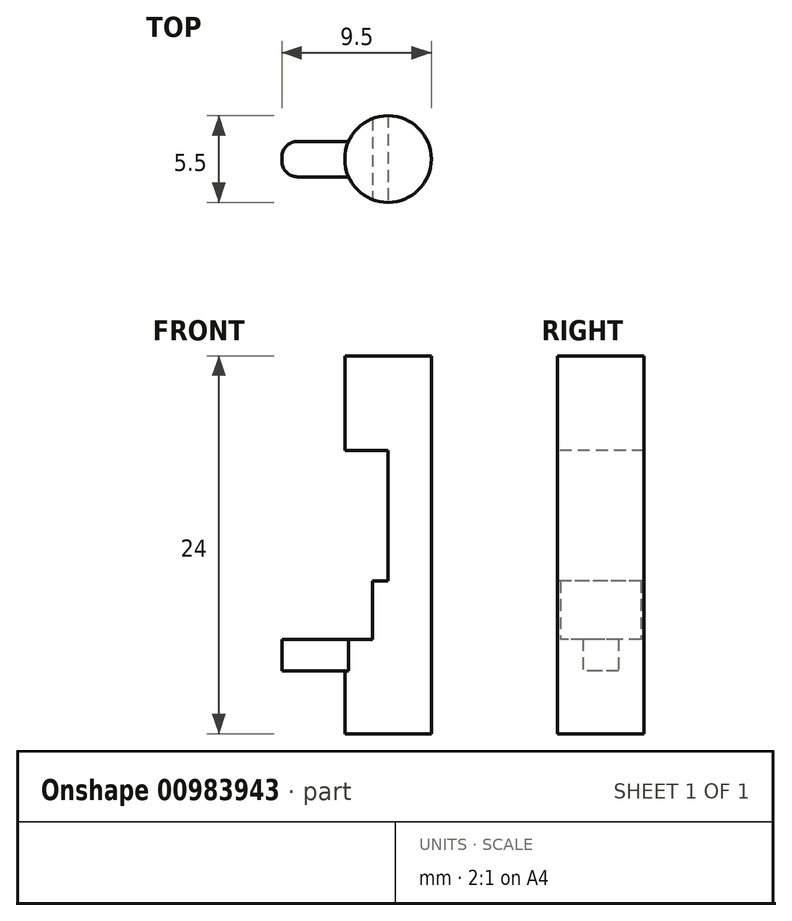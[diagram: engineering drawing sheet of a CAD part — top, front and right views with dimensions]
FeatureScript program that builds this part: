
annotation { "Feature Type Name" : "Feature", "Feature Type Description" : "" }
export const myFeature = defineFeature(function(context is Context, id is Id, definition is map)
    precondition{}
    {
        {
            var Q0;
            Q0=qCreatedBy(makeId("Top.planeOp"),FACE);
            var sketch = newSketch(context, id + "F0", { "sketchPlane" : qUnion([Q0])});
            skCircle(sketch, "E0", {"center": v(0, 0) * mm, "radius": 2.75 * mm});
            skLineSegment(sketch, "E1", {"start": v(0, 2.75) * mm, "end": v(0, -2.75) * mm});
            skLineSegment(sketch, "E2", {"start": v(-1, 2.56) * mm, "end": v(-1, -2.56) * mm});
            skLineSegment(sketch, "E3", {"start": v(0, 0) * mm, "end": v(0, 1.12) * mm});
            skLineSegment(sketch, "E4", {"start": v(0, 1.12) * mm, "end": v(-6.75, 1.12) * mm});
            skLineSegment(sketch, "E5", {"start": v(-6.75, 1.12) * mm, "end": v(-6.75, -1.13) * mm});
            skLineSegment(sketch, "E6", {"start": v(-6.75, -1.13) * mm, "end": v(0, -1.13) * mm});
            skSolve(sketch);
        }
        {
            var Q0;
            {var subQ0=sQuery(id+"F0.wireOp",EDGE,"E1");var subQ1=makeQuery(id+"F0.imprint","IMPRINT",VERTEX,{"derivedFrom":subQ0});Q0=makeQuery(id+"F0.imprint","IMPRINT",FACE,{"disambiguationData":[TD([[makeQuery(id+"F0.imprint","IMPRINT",EDGE,{"disambiguationData":[TD([[subQ1,-1.0]])],"derivedFrom":subQ0}),1.0]])]});}
            var Q1;
            {var subQ0=sQuery(id+"F0.wireOp",EDGE,"E2");var subQ1=sQuery(id+"F0.wireOp",EDGE,"E0");var subQ2=makeQuery(id+"F0.imprint","INTERSECT",VERTEX,{"disambiguationData":[OD(0.0)],"derivedFrom":[subQ1,subQ0]});var subQ3=sQuery(id+"F0.wireOp",EDGE,"E1");var subQ8=makeQuery(id+"F0.imprint","INTERSECT",VERTEX,{"disambiguationData":[OD(0.0)],"derivedFrom":[subQ1,subQ3]});Q1=qUnion([makeQuery(id+"F0.imprint","IMPRINT",FACE,{"disambiguationData":[TD([[makeQuery(id+"F0.imprint","IMPRINT",EDGE,{"disambiguationData":[TD([[subQ8,-1.0]])],"derivedFrom":subQ1}),1.0]])]}),makeQuery(id+"F0.imprint","IMPRINT",FACE,{"disambiguationData":[TD([[makeQuery(id+"F0.imprint","IMPRINT",EDGE,{"disambiguationData":[TD([[subQ2,-1.0]])],"derivedFrom":subQ1}),1.0]])]})]);}
            var Q2;
            {var subQ0=sQuery(id+"F0.wireOp",EDGE,"E1");var subQ1=sQuery(id+"F0.wireOp",EDGE,"E0");var subQ2=makeQuery(id+"F0.imprint","INTERSECT",VERTEX,{"disambiguationData":[OD(0.0)],"derivedFrom":[subQ1,subQ0]});Q2=makeQuery(id+"F0.imprint","IMPRINT",FACE,{"disambiguationData":[TD([[makeQuery(id+"F0.imprint","IMPRINT",EDGE,{"disambiguationData":[TD([[subQ2,-1.0]])],"derivedFrom":subQ1}),1.0]])]});}
            var Q3;
            {var subQ0=sQuery(id+"F0.wireOp",EDGE,"E2");var subQ1=sQuery(id+"F0.wireOp",EDGE,"E0");var subQ2=makeQuery(id+"F0.imprint","INTERSECT",VERTEX,{"disambiguationData":[OD(0.0)],"derivedFrom":[subQ1,subQ0]});var subQ6=sQuery(id+"F0.wireOp",EDGE,"E4");var subQ7=makeQuery(id+"F0.imprint","INTERSECT",VERTEX,{"derivedFrom":[subQ1,subQ6]});Q3=qUnion([makeQuery(id+"F0.imprint","IMPRINT",FACE,{"disambiguationData":[TD([[makeQuery(id+"F0.imprint","IMPRINT",EDGE,{"disambiguationData":[TD([[subQ7,1.0]])],"derivedFrom":subQ1}),1.0]])]}),makeQuery(id+"F0.imprint","IMPRINT",FACE,{"disambiguationData":[TD([[makeQuery(id+"F0.imprint","IMPRINT",EDGE,{"disambiguationData":[TD([[subQ2,1.0]])],"derivedFrom":subQ1}),1.0]])]})]);}
            var Q4;
            {var subQ3=sQuery(id+"F0.wireOp",EDGE,"E1");var subQ7=makeQuery(id+"F0.imprint","IMPRINT",VERTEX,{"derivedFrom":subQ3});Q4=makeQuery(id+"F0.imprint","IMPRINT",FACE,{"disambiguationData":[TD([[makeQuery(id+"F0.imprint","IMPRINT",EDGE,{"disambiguationData":[TD([[subQ7,-1.0]])],"derivedFrom":subQ3}),-1.0]])]});}
            var Q5;
            {var subQ0=sQuery(id+"F0.wireOp",EDGE,"E4");var subQ1=sQuery(id+"F0.wireOp",EDGE,"E0");var subQ2=makeQuery(id+"F0.imprint","INTERSECT",VERTEX,{"derivedFrom":[subQ1,subQ0]});Q5=makeQuery(id+"F0.imprint","IMPRINT",FACE,{"disambiguationData":[TD([[makeQuery(id+"F0.imprint","IMPRINT",EDGE,{"disambiguationData":[TD([[subQ2,-1.0]])],"derivedFrom":subQ1}),1.0]])]});}
            extrude(context, id + "F1", {"entities" : qUnion([Q0, Q1, Q2, Q3, Q4, Q5]), "depth" : 24 * mm, "offsetDistance" : 25 * mm});
        }
        {
            var Q0;
            {var subQ0=sQuery(id+"F0.wireOp",EDGE,"E2");var subQ1=sQuery(id+"F0.wireOp",EDGE,"E0");var subQ2=makeQuery(id+"F0.imprint","INTERSECT",VERTEX,{"disambiguationData":[OD(0.0)],"derivedFrom":[subQ1,subQ0]});var subQ3=sQuery(id+"F0.wireOp",EDGE,"E1");var subQ8=makeQuery(id+"F0.imprint","INTERSECT",VERTEX,{"disambiguationData":[OD(0.0)],"derivedFrom":[subQ1,subQ3]});Q0=qUnion([makeQuery(id+"F0.imprint","IMPRINT",FACE,{"disambiguationData":[TD([[makeQuery(id+"F0.imprint","IMPRINT",EDGE,{"disambiguationData":[TD([[subQ8,-1.0]])],"derivedFrom":subQ1}),1.0]])]}),makeQuery(id+"F0.imprint","IMPRINT",FACE,{"disambiguationData":[TD([[makeQuery(id+"F0.imprint","IMPRINT",EDGE,{"disambiguationData":[TD([[subQ2,-1.0]])],"derivedFrom":subQ1}),1.0]])]})]);}
            var Q1;
            {var subQ0=sQuery(id+"F0.wireOp",EDGE,"E1");var subQ1=sQuery(id+"F0.wireOp",EDGE,"E0");var subQ2=makeQuery(id+"F0.imprint","INTERSECT",VERTEX,{"disambiguationData":[OD(0.0)],"derivedFrom":[subQ1,subQ0]});Q1=makeQuery(id+"F0.imprint","IMPRINT",FACE,{"disambiguationData":[TD([[makeQuery(id+"F0.imprint","IMPRINT",EDGE,{"disambiguationData":[TD([[subQ2,-1.0]])],"derivedFrom":subQ1}),1.0]])]});}
            var Q2;
            {var subQ0=sQuery(id+"F0.wireOp",EDGE,"E2");var subQ1=sQuery(id+"F0.wireOp",EDGE,"E0");var subQ2=makeQuery(id+"F0.imprint","INTERSECT",VERTEX,{"disambiguationData":[OD(0.0)],"derivedFrom":[subQ1,subQ0]});var subQ6=sQuery(id+"F0.wireOp",EDGE,"E4");var subQ7=makeQuery(id+"F0.imprint","INTERSECT",VERTEX,{"derivedFrom":[subQ1,subQ6]});Q2=qUnion([makeQuery(id+"F0.imprint","IMPRINT",FACE,{"disambiguationData":[TD([[makeQuery(id+"F0.imprint","IMPRINT",EDGE,{"disambiguationData":[TD([[subQ7,1.0]])],"derivedFrom":subQ1}),1.0]])]}),makeQuery(id+"F0.imprint","IMPRINT",FACE,{"disambiguationData":[TD([[makeQuery(id+"F0.imprint","IMPRINT",EDGE,{"disambiguationData":[TD([[subQ2,1.0]])],"derivedFrom":subQ1}),1.0]])]})]);}
            var Q3;
            {var subQ3=sQuery(id+"F0.wireOp",EDGE,"E1");var subQ7=makeQuery(id+"F0.imprint","IMPRINT",VERTEX,{"derivedFrom":subQ3});Q3=makeQuery(id+"F0.imprint","IMPRINT",FACE,{"disambiguationData":[TD([[makeQuery(id+"F0.imprint","IMPRINT",EDGE,{"disambiguationData":[TD([[subQ7,-1.0]])],"derivedFrom":subQ3}),-1.0]])]});}
            var Q4;
            {var subQ0=sQuery(id+"F0.wireOp",EDGE,"E4");var subQ1=sQuery(id+"F0.wireOp",EDGE,"E0");var subQ2=makeQuery(id+"F0.imprint","INTERSECT",VERTEX,{"derivedFrom":[subQ1,subQ0]});Q4=makeQuery(id+"F0.imprint","IMPRINT",FACE,{"disambiguationData":[TD([[makeQuery(id+"F0.imprint","IMPRINT",EDGE,{"disambiguationData":[TD([[subQ2,-1.0]])],"derivedFrom":subQ1}),1.0]])]});}
            extrude(context, id + "F2", {"entities" : qUnion([Q0, Q1, Q2, Q3, Q4]), "operationType" : NewBodyOperationType.REMOVE, "depth" : 18 * mm, "offsetDistance" : 25 * mm});
        }
        {
            var Q0;
            {var subQ0=sQuery(id+"F0.wireOp",EDGE,"E2");var subQ1=sQuery(id+"F0.wireOp",EDGE,"E0");var subQ2=makeQuery(id+"F0.imprint","INTERSECT",VERTEX,{"disambiguationData":[OD(0.0)],"derivedFrom":[subQ1,subQ0]});var subQ3=sQuery(id+"F0.wireOp",EDGE,"E1");var subQ8=makeQuery(id+"F0.imprint","INTERSECT",VERTEX,{"disambiguationData":[OD(0.0)],"derivedFrom":[subQ1,subQ3]});Q0=qUnion([makeQuery(id+"F0.imprint","IMPRINT",FACE,{"disambiguationData":[TD([[makeQuery(id+"F0.imprint","IMPRINT",EDGE,{"disambiguationData":[TD([[subQ8,-1.0]])],"derivedFrom":subQ1}),1.0]])]}),makeQuery(id+"F0.imprint","IMPRINT",FACE,{"disambiguationData":[TD([[makeQuery(id+"F0.imprint","IMPRINT",EDGE,{"disambiguationData":[TD([[subQ2,-1.0]])],"derivedFrom":subQ1}),1.0]])]})]);}
            var Q1;
            {var subQ3=sQuery(id+"F0.wireOp",EDGE,"E1");var subQ7=makeQuery(id+"F0.imprint","IMPRINT",VERTEX,{"derivedFrom":subQ3});Q1=makeQuery(id+"F0.imprint","IMPRINT",FACE,{"disambiguationData":[TD([[makeQuery(id+"F0.imprint","IMPRINT",EDGE,{"disambiguationData":[TD([[subQ7,-1.0]])],"derivedFrom":subQ3}),-1.0]])]});}
            extrude(context, id + "F3", {"entities" : qUnion([Q0, Q1]), "operationType" : NewBodyOperationType.ADD, "depth" : 9.7 * mm, "offsetDistance" : 25 * mm});
        }
        {
            var Q0;
            {var subQ0=sQuery(id+"F0.wireOp",EDGE,"E2");var subQ1=sQuery(id+"F0.wireOp",EDGE,"E0");var subQ2=makeQuery(id+"F0.imprint","INTERSECT",VERTEX,{"disambiguationData":[OD(0.0)],"derivedFrom":[subQ1,subQ0]});var subQ6=sQuery(id+"F0.wireOp",EDGE,"E4");var subQ7=makeQuery(id+"F0.imprint","INTERSECT",VERTEX,{"derivedFrom":[subQ1,subQ6]});Q0=qUnion([makeQuery(id+"F0.imprint","IMPRINT",FACE,{"disambiguationData":[TD([[makeQuery(id+"F0.imprint","IMPRINT",EDGE,{"disambiguationData":[TD([[subQ7,1.0]])],"derivedFrom":subQ1}),1.0]])]}),makeQuery(id+"F0.imprint","IMPRINT",FACE,{"disambiguationData":[TD([[makeQuery(id+"F0.imprint","IMPRINT",EDGE,{"disambiguationData":[TD([[subQ2,1.0]])],"derivedFrom":subQ1}),1.0]])]})]);}
            var Q1;
            {var subQ0=sQuery(id+"F0.wireOp",EDGE,"E4");var subQ1=sQuery(id+"F0.wireOp",EDGE,"E0");var subQ2=makeQuery(id+"F0.imprint","INTERSECT",VERTEX,{"derivedFrom":[subQ1,subQ0]});Q1=makeQuery(id+"F0.imprint","IMPRINT",FACE,{"disambiguationData":[TD([[makeQuery(id+"F0.imprint","IMPRINT",EDGE,{"disambiguationData":[TD([[subQ2,-1.0]])],"derivedFrom":subQ1}),1.0]])]});}
            extrude(context, id + "F4", {"entities" : qUnion([Q0, Q1]), "operationType" : NewBodyOperationType.ADD, "depth" : 6 * mm, "offsetDistance" : 25 * mm});
        }
        {
            var Q0;
            {var subQ5=sQuery(id+"F0.wireOp",EDGE,"E5");Q0=makeQuery(id+"F0.imprint","IMPRINT",FACE,{"disambiguationData":[TD([[makeQuery(id+"F0.imprint","IMPRINT",EDGE,{"derivedFrom":subQ5}),1.0]])]});}
            extrude(context, id + "F5", {"entities" : qUnion([Q0]), "operationType" : NewBodyOperationType.ADD, "depth" : 6 * mm, "offsetDistance" : 25 * mm});
        }
        {
            var Q0;
            Q0=makeQuery(id+"F5.opExtrude","SWEPT_EDGE",EDGE,{"disambiguationData":[OSD([sQuery(id+"F0.wireOp",EDGE,"E4"),sQuery(id+"F0.wireOp",EDGE,"E5")])]});
            var Q1;
            Q1=makeQuery(id+"F5.opExtrude","SWEPT_EDGE",EDGE,{"disambiguationData":[OSD([sQuery(id+"F0.wireOp",EDGE,"E5"),sQuery(id+"F0.wireOp",EDGE,"E6")])]});
            fillet(context, id + "F6", {"entities" : qUnion([Q0, Q1]), "radius" : 1 * mm, "tangentPropagation" : true, "allowEdgeOverflow" : false});
        }
        {
            var Q0;
            {var subQ5=sQuery(id+"F0.wireOp",EDGE,"E5");Q0=makeQuery(id+"F0.imprint","IMPRINT",FACE,{"disambiguationData":[TD([[makeQuery(id+"F0.imprint","IMPRINT",EDGE,{"derivedFrom":subQ5}),1.0]])]});}
            extrude(context, id + "F7", {"entities" : qUnion([Q0]), "operationType" : NewBodyOperationType.REMOVE, "depth" : 4 * mm, "offsetDistance" : 25 * mm});
        }
    });
